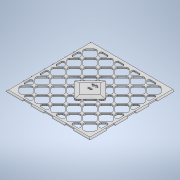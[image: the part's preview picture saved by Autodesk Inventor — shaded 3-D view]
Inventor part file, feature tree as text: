
AUTODESK INVENTOR PART (.ipt)
format: ipt  version: 2020 (Build 240168000, 168)  size: 1,244,160 bytes
history: native  units: in
note: dims shown in document units (in); Inventor stores cm internally (conversion verified against a paired STEP export)
features: sketch x5, extrude x4, chamfer x4, fillet x3, emboss x1
ambient origin geometry x8: Origin, YZ Plane, XZ Plane, XY Plane, X Axis, Y Axis, Z Axis, Center Point
bodies: Solid1 (feature_tree)
feature tree (17):
  extrude  "Extrusion1"  Depth=3.937in
  extrude  "Extrusion2"  Depth=0.0591in
  chamfer  "Chamfer1"  Distance=0.0591in
  chamfer  "Chamfer2"  Distance=0.0394in
  chamfer  "Chamfer3"  Distance=0.0394in
  chamfer  "Chamfer4"  Distance=0.748in
  extrude  "Extrusion3"  Depth=0.1181in
  fillet  "Fillet1"  Radius=0.0394in
  fillet  "Fillet2"  Radius=1.9685in
  extrude  "Extrusion4"  Depth=0.1181in
  fillet  "Fillet4"  Radius=1.5748in
  emboss  "Emboss1"
  sketch  "Sketch1"  dims[d0=3.937in d1=3.937in]
  sketch  "Sketch2"  dims[d2=0.0591in d3=0.0591in]
  sketch  "Sketch3"  dims[d4=0.0394in]
  sketch  "Sketch4"  dims[d5=0.0394in]
  sketch  "Sketch5"  dims[d6=0.0591in d7=0.0591in d8=0.0394in d9=0.0394in d10=0.748in d11=0.748in d12=0.0394in d13=1.9685in d15=0.748in d16=1.9685in d18=0.748in d21=0.0394in d22=1.5748in d24=0.748in d25=1.5748in d27=0.748in d30=1.5748in d32=0.748in d33=0.3937in d35=1.0in d37=1.5748in d39=0.748in d40=0.3937in d42=1.0in d44=0.0394in d45=0.0787in d46=1.5748in d48=0.748in d49=0.3937in d51=1.0in d53=1.5748in d55=0.748in d56=0.3937in d58=1.0in d60=0.0591in d61=0.0in d62=0.0591in d63=0.0in d64=0.1969in d65=0.0591in d66=45.0deg d67=0.1969in d68=0.0591in d69=45.0deg d70=0.1969in d71=0.0591in d72=45.0deg d73=0.1969in d74=0.0591in d75=45.0deg d76=0.0984in d77=0.0984in d78=0.0591in d79=0.0591in d80=0.1181in d81=0.0in d82=0.0787in d83=0.0197in d84=0.9843in d85=0.9843in d86=0.9843in d87=0.9843in d88=0.1969in d89=0.0591in d90=0.3937in d91=0.1969in d92=0.0591in d93=0.3937in d94=0.1969in d95=0.3937in d96=0.0591in d97=0.3937in d98=0.0591in d99=0.3937in d100=0.0591in d101=0.3937in d102=0.9843in d103=0.9843in d104=0.1969in d105=0.3937in d106=0.0591in d107=0.9843in d108=0.1969in d109=0.3937in d110=0.0591in d111=0.1969in d112=0.3937in d113=0.0591in d114=0.0591in d115=0.0in d117=0.0591in d118=0.1181in d119=0.0in]
